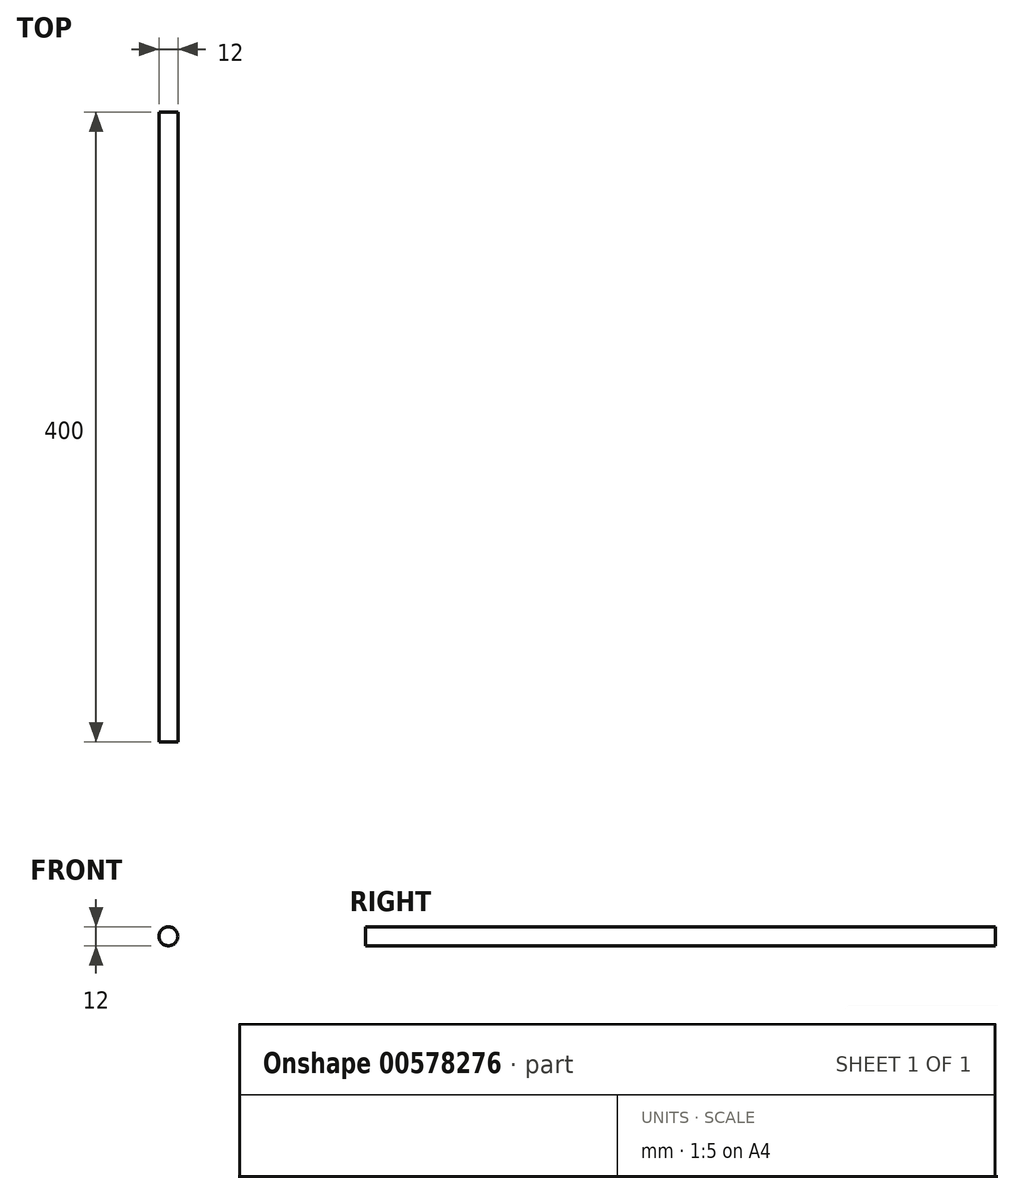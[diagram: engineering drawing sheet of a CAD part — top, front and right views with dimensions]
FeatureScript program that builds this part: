
annotation { "Feature Type Name" : "Feature", "Feature Type Description" : "" }
export const myFeature = defineFeature(function(context is Context, id is Id, definition is map)
    precondition{}
    {
        {
            var Q0;
            Q0=qCreatedBy(makeId("Front.planeOp"),FACE);
            var sketch = newSketch(context, id + "F0", { "sketchPlane" : qUnion([Q0])});
            skCircle(sketch, "E0", {"center": v(0, 0) * mm, "radius": 6 * mm});
            skSolve(sketch);
        }
        {
            var Q0;
            Q0 = qSketchRegion(id + "F0", true);
            extrude(context, id + "F1", {"entities" : qUnion([Q0]), "depth" : 400 * mm, "offsetDistance" : 25 * mm});
        }
    });
